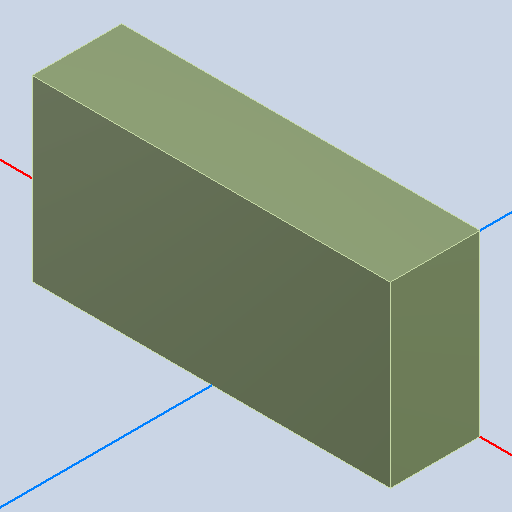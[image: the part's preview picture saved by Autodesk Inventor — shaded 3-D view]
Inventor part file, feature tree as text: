
AUTODESK INVENTOR PART (.ipt)
format: ipt  version: 2022 (Build 260153000, 153)  size: 94,208 bytes
history: native  units: mm
features: other x2, extrude x1
ambient origin geometry x8: Origin, YZ Plane, XZ Plane, XY Plane, X Axis, Y Axis, Z Axis, Center Point
bodies: Body1 (feature_tree)
feature tree (3):
  other  "Твердое тело1"
  extrude  "Выдавливание1"  Depth=1.0mm TaperAngle=0.0deg
  other  "M0805, M0805_1"
